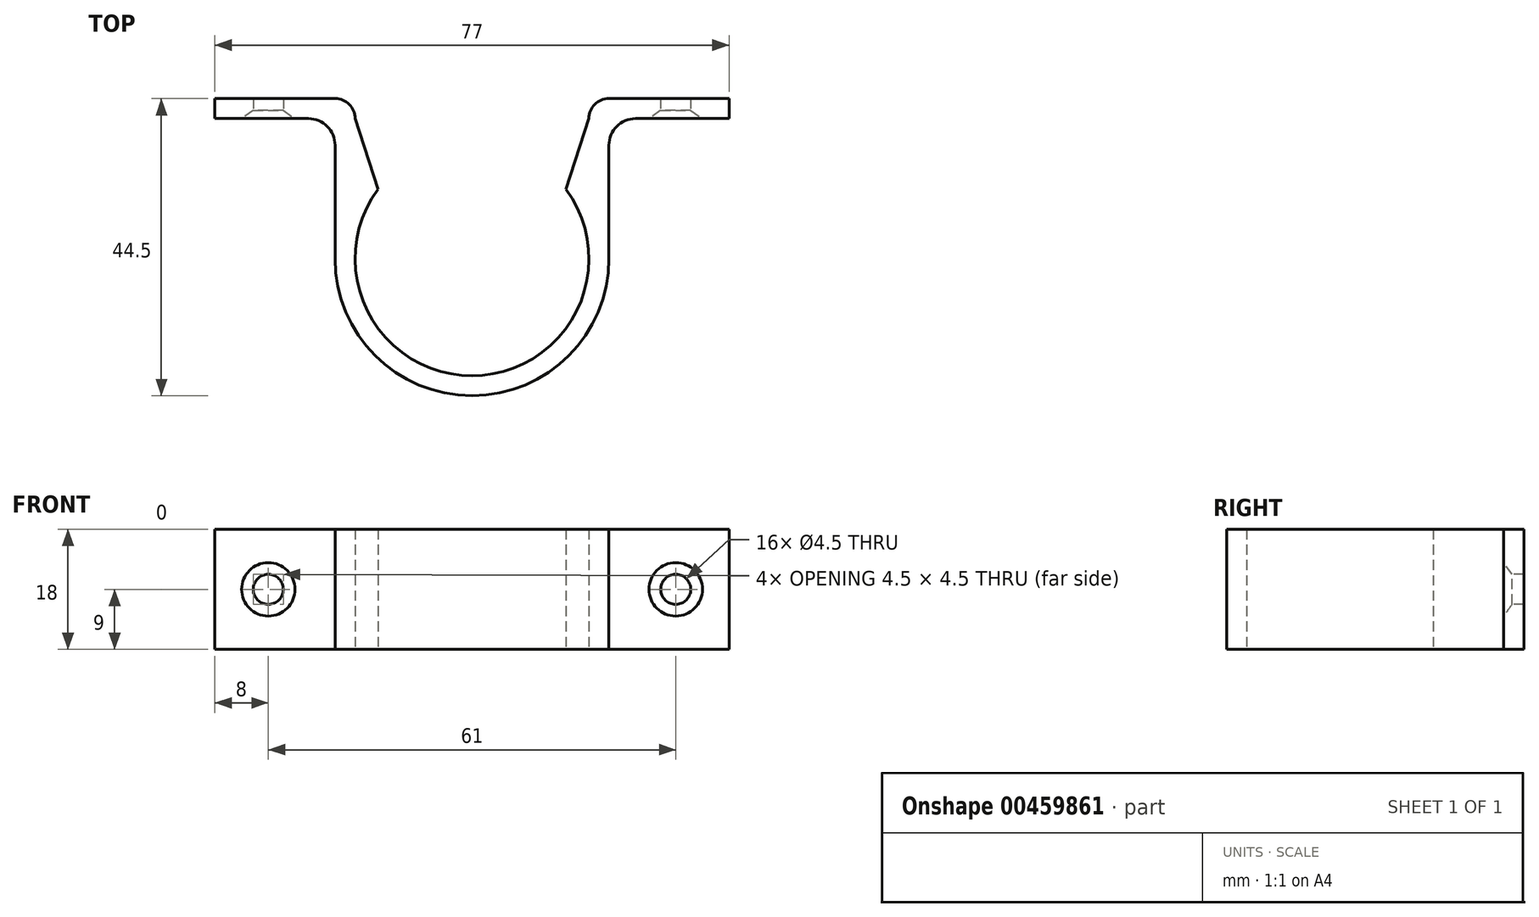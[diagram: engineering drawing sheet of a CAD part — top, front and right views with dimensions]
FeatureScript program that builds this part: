
annotation { "Feature Type Name" : "Feature", "Feature Type Description" : "" }
export const myFeature = defineFeature(function(context is Context, id is Id, definition is map)
    precondition{}
    {
        {
            var Q0;
            Q0=qCreatedBy(makeId("Top.planeOp"),FACE);
            var sketch = newSketch(context, id + "F0", { "sketchPlane" : qUnion([Q0])});
            skLineSegment(sketch, "E0", {"start": v(-38.5, 0) * mm, "end": v(-20.5, 0) * mm});
            skLineSegment(sketch, "E1", {"start": v(-38.5, -3) * mm, "end": v(-24.5, -3) * mm});
            skLineSegment(sketch, "E2", {"start": v(-38.5, 0) * mm, "end": v(-38.5, -3) * mm});
            skLineSegment(sketch, "E3.MirrorCS", {"start": v(38.5, 0) * mm, "end": v(20.5, 0) * mm});
            skLineSegment(sketch, "E4.MirrorCS", {"start": v(38.5, 0) * mm, "end": v(38.5, -3) * mm});
            skLineSegment(sketch, "E5.MirrorCS", {"start": v(38.5, -3) * mm, "end": v(24.5, -3) * mm});
            skLineSegment(sketch, "E6", {"start": v(-20.5, -7) * mm, "end": v(-20.5, -24) * mm});
            skLineSegment(sketch, "E7", {"start": v(-17.5, -24) * mm, "end": v(17.5, -24) * mm, "construction": true});
            skLineSegment(sketch, "E8.MirrorCS", {"start": v(20.5, -7) * mm, "end": v(20.5, -24) * mm});
            skArc(sketch, "E9", {"start": v(-20.5, -24) * mm, "mid": v(0, -44.5) * mm, "end": v(20.5, -24) * mm});
            skPoint(sketch, "E10.visualSharp", {"position": v(-20.5, -3) * mm});
            skArc(sketch, "E10.filletArc", {"start": v(-20.5, -7) * mm, "mid": v(-21.67, -4.17) * mm, "end": v(-24.5, -3) * mm});
            skPoint(sketch, "E11.visualSharp", {"position": v(-17.5, 0) * mm});
            skArc(sketch, "E11.filletArc", {"start": v(-17.5, -3) * mm, "mid": v(-18.38, -0.88) * mm, "end": v(-20.5, 0) * mm});
            skPoint(sketch, "E12.visualSharp", {"position": v(17.5, 0) * mm});
            skArc(sketch, "E12.filletArc", {"start": v(20.5, 0) * mm, "mid": v(18.38, -0.88) * mm, "end": v(17.5, -3) * mm});
            skArc(sketch, "E13.filletArc", {"start": v(24.5, -3) * mm, "mid": v(21.67, -4.17) * mm, "end": v(20.5, -7) * mm});
            skArc(sketch, "E14", {"start": v(-14.06, -13.58) * mm, "mid": v(0, -41.5) * mm, "end": v(14.06, -13.58) * mm});
            skLineSegment(sketch, "E15", {"start": v(14.06, -13.58) * mm, "end": v(17.5, -3) * mm});
            skLineSegment(sketch, "E16.MirrorCS", {"start": v(-14.06, -13.58) * mm, "end": v(-17.5, -3) * mm});
            skPoint(sketch, "E17.MirrorCS.start.orphan", {"position": v(17.5, -24) * mm});
            skSolve(sketch);
        }
        {
            var Q0;
            Q0=makeQuery(id+"F0.imprint","IMPRINT",FACE,{"disambiguationData":[TD([[makeQuery(id+"F0.imprint","IMPRINT",EDGE,{"derivedFrom":sQuery(id+"F0.wireOp",EDGE,"E0")}),-1.0]])]});
            extrude(context, id + "F1", {"entities" : qUnion([Q0]), "depth" : 18 * mm});
        }
        {
            var Q0;
            Q0=makeQuery(id+"F1.opExtrude","SWEPT_FACE",FACE,{"disambiguationData":[OSD([sQuery(id+"F0.wireOp",EDGE,"E1")])]});
            var sketch = newSketch(context, id + "F2", { "sketchPlane" : qUnion([Q0])});
            skPoint(sketch, "E18", {"position": v(-30.5, 9) * mm});
            skPoint(sketch, "E19.MirrorP", {"position": v(30.5, 9) * mm});
            skSolve(sketch);
        }
        {
            var Q0;
            Q0=sQuery(id+"F2.wireOp",VERTEX,"E18");
            var Q1;
            Q1=sQuery(id+"F2.wireOp",VERTEX,"E19.MirrorP");
            var Q2;
            Q2=makeQuery(id+"F1.opExtrude","SWEPT_BODY",BODY,{"disambiguationData":[OSD([sQuery(id+"F0.wireOp",EDGE,"E0"),sQuery(id+"F0.wireOp",EDGE,"E1"),sQuery(id+"F0.wireOp",EDGE,"E2"),sQuery(id+"F0.wireOp",EDGE,"E3.MirrorCS"),sQuery(id+"F0.wireOp",EDGE,"E4.MirrorCS"),sQuery(id+"F0.wireOp",EDGE,"E5.MirrorCS"),sQuery(id+"F0.wireOp",EDGE,"AOmZp6DZ-lfay-bdt2-fHSV-ltmR5s5c6Mpa"),sQuery(id+"F0.wireOp",EDGE,"JaN8iGJh-GyLW-BEKW-BNss-tCEKeWj3Zmzy"),sQuery(id+"F0.wireOp",EDGE,"E6"),sQuery(id+"F0.wireOp",EDGE,"E17.MirrorCS"),sQuery(id+"F0.wireOp",EDGE,"E8.MirrorCS"),sQuery(id+"F0.wireOp",EDGE,"E9"),sQuery(id+"F0.wireOp",EDGE,"E10.filletArc"),sQuery(id+"F0.wireOp",EDGE,"E11.filletArc"),sQuery(id+"F0.wireOp",EDGE,"E12.filletArc"),sQuery(id+"F0.wireOp",EDGE,"E13.filletArc")])]});
            hole(context, id + "F3", {"style" : HoleStyle.C_SINK, "endStyle" : HoleEndStyle.THROUGH, "standardTappedOrClearance" : lookupTablePath({ "standard" : "ISO", "size" : "4.5", "type" : "Drilled" }), "standardBlindInLast" : lookupTablePath({ "standard" : "ISO", "size" : "4.5", "type" : "Drilled" }), "holeDiameter" : 4.5 * mm, "cSinkDiameter" : 8 * mm, "cSinkAngle" : 110 * degree, "startFromSketch" : true, "locations" : qUnion([Q0, Q1]), "scope" : qUnion([Q2]), "isTappedThrough" : true});
        }
    });
